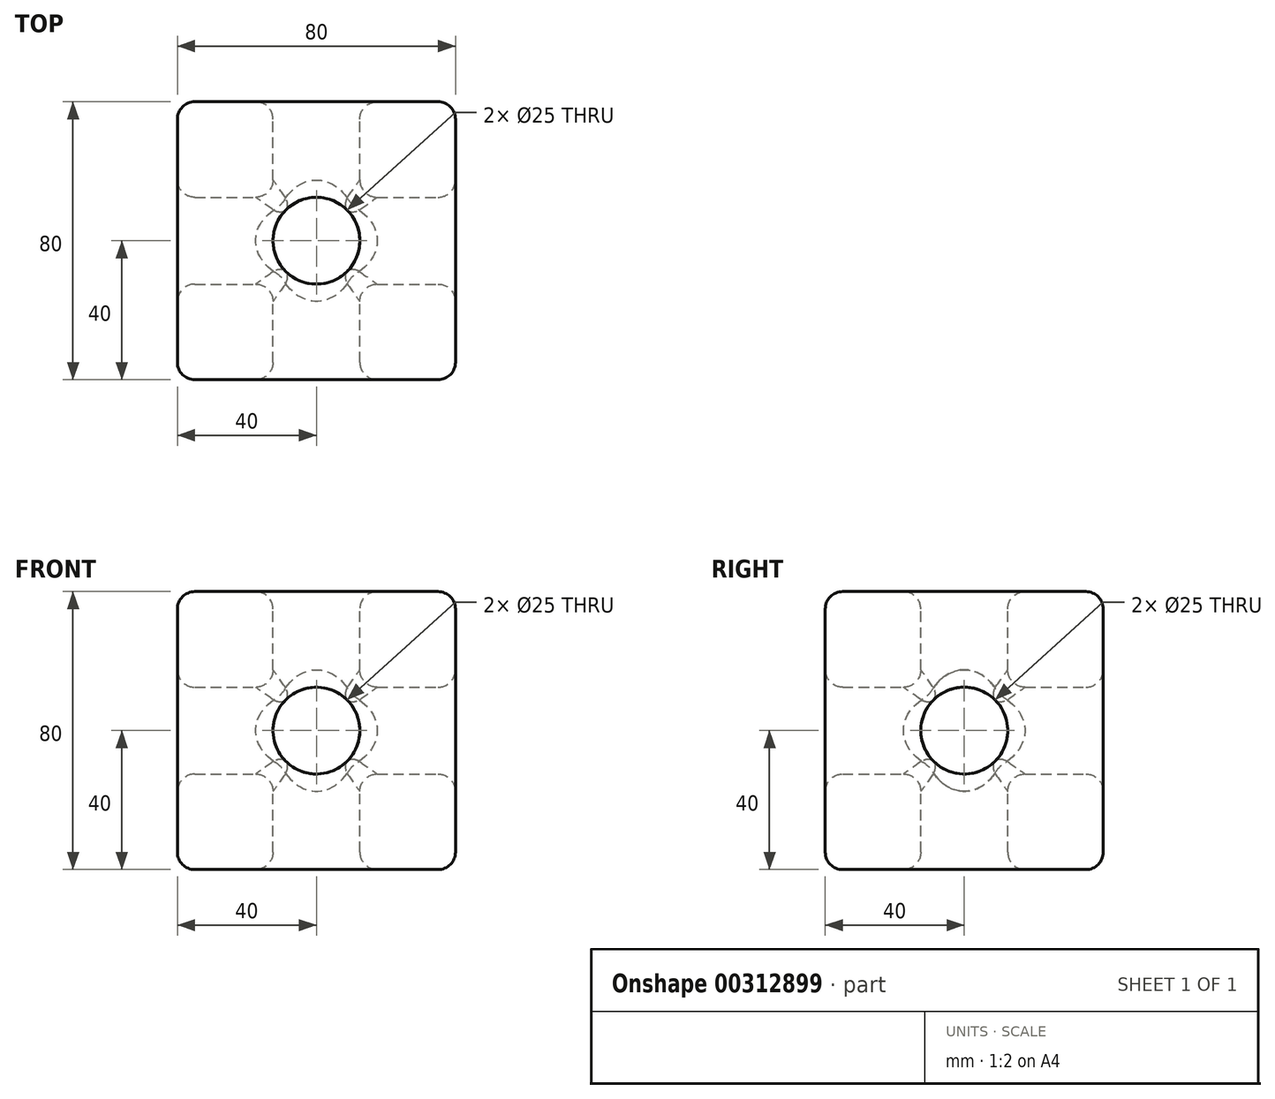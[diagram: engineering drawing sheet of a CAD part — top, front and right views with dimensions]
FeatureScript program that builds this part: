
annotation { "Feature Type Name" : "Feature", "Feature Type Description" : "" }
export const myFeature = defineFeature(function(context is Context, id is Id, definition is map)
    precondition{}
    {
        {
            var Q0;
            Q0=qCreatedBy(makeId("Top.planeOp"),FACE);
            var sketch = newSketch(context, id + "F0", { "sketchPlane" : qUnion([Q0])});
            skLineSegment(sketch, "E0.bottom", {"start": v(40, -40) * mm, "end": v(-40, -40) * mm});
            skLineSegment(sketch, "E0.top", {"start": v(40, 40) * mm, "end": v(-40, 40) * mm});
            skLineSegment(sketch, "E0.left", {"start": v(40, -40) * mm, "end": v(40, 40) * mm});
            skLineSegment(sketch, "E0.right", {"start": v(-40, -40) * mm, "end": v(-40, 40) * mm});
            skPoint(sketch, "E0.middle", {"position": v(0, 0) * mm});
            skSolve(sketch);
        }
        {
            var Q0;
            Q0=makeQuery(id+"F0.imprint","IMPRINT",FACE,{"disambiguationData":[TD([[makeQuery(id+"F0.imprint","IMPRINT",EDGE,{"derivedFrom":sQuery(id+"F0.wireOp",EDGE,"E0.bottom")}),-1.0]])]});
            extrude(context, id + "F1", {"entities" : qUnion([Q0]), "endBound" : BoundingType.SYMMETRIC, "depth" : 80 * mm});
        }
        {
            var Q0;
            Q0=makeQuery(id+"F1.opExtrude","SWEPT_EDGE",EDGE,{"disambiguationData":[OSD([sQuery(id+"F0.wireOp",EDGE,"E0.top"),sQuery(id+"F0.wireOp",EDGE,"E0.left")])]});
            var Q1;
            Q1=makeQuery(id+"F1.opExtrude","CAP_EDGE",EDGE,{"disambiguationData":[OSD([sQuery(id+"F0.wireOp",EDGE,"E0.top")])],"isStart":false});
            var Q2;
            Q2=makeQuery(id+"F1.opExtrude","SWEPT_EDGE",EDGE,{"disambiguationData":[OSD([sQuery(id+"F0.wireOp",EDGE,"E0.top"),sQuery(id+"F0.wireOp",EDGE,"E0.right")])]});
            var Q3;
            Q3=makeQuery(id+"F1.opExtrude","CAP_EDGE",EDGE,{"disambiguationData":[OSD([sQuery(id+"F0.wireOp",EDGE,"E0.top")])],"isStart":true});
            var Q4;
            Q4=makeQuery(id+"F1.opExtrude","SWEPT_EDGE",EDGE,{"disambiguationData":[OSD([sQuery(id+"F0.wireOp",EDGE,"E0.bottom"),sQuery(id+"F0.wireOp",EDGE,"E0.left")])]});
            var Q5;
            Q5=makeQuery(id+"F1.opExtrude","CAP_EDGE",EDGE,{"disambiguationData":[OSD([sQuery(id+"F0.wireOp",EDGE,"E0.left")])],"isStart":true});
            var Q6;
            Q6=makeQuery(id+"F1.opExtrude","CAP_EDGE",EDGE,{"disambiguationData":[OSD([sQuery(id+"F0.wireOp",EDGE,"E0.right")])],"isStart":false});
            var Q7;
            Q7=makeQuery(id+"F1.opExtrude","SWEPT_EDGE",EDGE,{"disambiguationData":[OSD([sQuery(id+"F0.wireOp",EDGE,"E0.bottom"),sQuery(id+"F0.wireOp",EDGE,"E0.right")])]});
            var Q8;
            Q8=makeQuery(id+"F1.opExtrude","CAP_EDGE",EDGE,{"disambiguationData":[OSD([sQuery(id+"F0.wireOp",EDGE,"E0.right")])],"isStart":true});
            var Q9;
            Q9=makeQuery(id+"F1.opExtrude","CAP_EDGE",EDGE,{"disambiguationData":[OSD([sQuery(id+"F0.wireOp",EDGE,"E0.bottom")])],"isStart":false});
            var Q10;
            Q10=makeQuery(id+"F1.opExtrude","CAP_EDGE",EDGE,{"disambiguationData":[OSD([sQuery(id+"F0.wireOp",EDGE,"E0.bottom")])],"isStart":true});
            var Q11;
            Q11=makeQuery(id+"F1.opExtrude","CAP_EDGE",EDGE,{"disambiguationData":[OSD([sQuery(id+"F0.wireOp",EDGE,"E0.left")])],"isStart":false});
            fillet(context, id + "F2", {"entities" : qUnion([Q0, Q1, Q2, Q3, Q4, Q5, Q6, Q7, Q8, Q9, Q10, Q11]), "radius" : 5 * mm, "tangentPropagation" : true, "allowEdgeOverflow" : false});
        }
        {
            var Q0;
            Q0=makeQuery(id+"F1.opExtrude","CAP_FACE",FACE,{"disambiguationData":[OSD([sQuery(id+"F0.wireOp",EDGE,"E0.bottom"),sQuery(id+"F0.wireOp",EDGE,"E0.top"),sQuery(id+"F0.wireOp",EDGE,"E0.left"),sQuery(id+"F0.wireOp",EDGE,"E0.right")])],"isStart":false});
            var sketch = newSketch(context, id + "F3", { "sketchPlane" : qUnion([Q0])});
            skCircle(sketch, "E1", {"center": v(0, 0) * mm, "radius": 12.5 * mm});
            skSolve(sketch);
        }
        {
            var Q0;
            Q0=makeQuery(id+"F3.imprint","IMPRINT",FACE,{"disambiguationData":[TD([[makeQuery(id+"F3.imprint","IMPRINT",EDGE,{"derivedFrom":sQuery(id+"F3.wireOp",EDGE,"E1")}),1.0]])]});
            extrude(context, id + "F4", {"entities" : qUnion([Q0]), "operationType" : NewBodyOperationType.REMOVE, "endBound" : BoundingType.THROUGH_ALL, "oppositeDirection" : true, "depth" : 25 * mm});
        }
        {
            var Q0;
            Q0=makeQuery(id+"F1.opExtrude","SWEPT_FACE",FACE,{"disambiguationData":[OSD([sQuery(id+"F0.wireOp",EDGE,"E0.left")])]});
            var sketch = newSketch(context, id + "F5", { "sketchPlane" : qUnion([Q0])});
            skCircle(sketch, "E2", {"center": v(0, 0) * mm, "radius": 12.5 * mm});
            skSolve(sketch);
        }
        {
            var Q0;
            Q0=makeQuery(id+"F5.imprint","IMPRINT",FACE,{"disambiguationData":[TD([[makeQuery(id+"F5.imprint","IMPRINT",EDGE,{"derivedFrom":sQuery(id+"F5.wireOp",EDGE,"E2")}),1.0]])]});
            extrude(context, id + "F6", {"entities" : qUnion([Q0]), "operationType" : NewBodyOperationType.REMOVE, "endBound" : BoundingType.THROUGH_ALL, "oppositeDirection" : true, "depth" : 25 * mm});
        }
        {
            var Q0;
            Q0=makeQuery(id+"F1.opExtrude","SWEPT_FACE",FACE,{"disambiguationData":[OSD([sQuery(id+"F0.wireOp",EDGE,"E0.top")])]});
            var sketch = newSketch(context, id + "F7", { "sketchPlane" : qUnion([Q0])});
            skCircle(sketch, "E3", {"center": v(0, 0) * mm, "radius": 12.5 * mm});
            skSolve(sketch);
        }
        {
            var Q0;
            Q0=makeQuery(id+"F7.imprint","IMPRINT",FACE,{"disambiguationData":[TD([[makeQuery(id+"F7.imprint","IMPRINT",EDGE,{"derivedFrom":sQuery(id+"F7.wireOp",EDGE,"E3")}),1.0]])]});
            extrude(context, id + "F8", {"entities" : qUnion([Q0]), "operationType" : NewBodyOperationType.REMOVE, "endBound" : BoundingType.THROUGH_ALL, "oppositeDirection" : true, "depth" : 25 * mm});
        }
        {
            var Q0;
            Q0=makeQuery(id+"F8.boolean.opBoolean","INTERSECT",EDGE,{"derivedFrom":[makeQuery(id+"F1.opExtrude","SWEPT_FACE",FACE,{"disambiguationData":[OSD([sQuery(id+"F0.wireOp",EDGE,"E0.bottom")])]}),makeQuery(id+"F8.opExtrude","SWEPT_FACE",FACE,{"disambiguationData":[OSD([sQuery(id+"F7.wireOp",EDGE,"E3")])]})]});
            var Q1;
            Q1=makeQuery(id+"F6.boolean.opBoolean","INTERSECT",EDGE,{"derivedFrom":[makeQuery(id+"F1.opExtrude","SWEPT_FACE",FACE,{"disambiguationData":[OSD([sQuery(id+"F0.wireOp",EDGE,"E0.right")])]}),makeQuery(id+"F6.opExtrude","SWEPT_FACE",FACE,{"disambiguationData":[OSD([sQuery(id+"F5.wireOp",EDGE,"E2")])]})]});
            var Q2;
            Q2=makeQuery(id+"F4.boolean.opBoolean","COPY",EDGE,{"derivedFrom":makeQuery(id+"F4.opExtrude","CAP_EDGE",EDGE,{"disambiguationData":[OSD([sQuery(id+"F3.wireOp",EDGE,"E1")])],"isStart":true})});
            var Q3;
            Q3=makeQuery(id+"F8.boolean.opBoolean","INTERSECT",EDGE,{"disambiguationData":[OD(3.0)],"derivedFrom":[makeQuery(id+"F4.boolean.opBoolean","COPY",FACE,{"derivedFrom":makeQuery(id+"F4.opExtrude","SWEPT_FACE",FACE,{"disambiguationData":[OSD([sQuery(id+"F3.wireOp",EDGE,"E1")])]})}),makeQuery(id+"F8.opExtrude","SWEPT_FACE",FACE,{"disambiguationData":[OSD([sQuery(id+"F7.wireOp",EDGE,"E3")])]})]});
            var Q4;
            Q4=makeQuery(id+"F8.boolean.opBoolean","COPY",EDGE,{"derivedFrom":makeQuery(id+"F8.opExtrude","CAP_EDGE",EDGE,{"disambiguationData":[OSD([sQuery(id+"F7.wireOp",EDGE,"E3")])],"isStart":true})});
            var Q5;
            Q5=makeQuery(id+"F6.boolean.opBoolean","COPY",EDGE,{"derivedFrom":makeQuery(id+"F6.opExtrude","CAP_EDGE",EDGE,{"disambiguationData":[OSD([sQuery(id+"F5.wireOp",EDGE,"E2")])],"isStart":true})});
            var Q6;
            Q6=makeQuery(id+"F4.boolean.opBoolean","INTERSECT",EDGE,{"derivedFrom":[makeQuery(id+"F1.opExtrude","CAP_FACE",FACE,{"disambiguationData":[OSD([sQuery(id+"F0.wireOp",EDGE,"E0.bottom"),sQuery(id+"F0.wireOp",EDGE,"E0.top"),sQuery(id+"F0.wireOp",EDGE,"E0.left"),sQuery(id+"F0.wireOp",EDGE,"E0.right")])],"isStart":true}),makeQuery(id+"F4.opExtrude","SWEPT_FACE",FACE,{"disambiguationData":[OSD([sQuery(id+"F3.wireOp",EDGE,"E1")])]})]});
            var Q7;
            Q7=makeQuery(id+"F8.boolean.opBoolean","INTERSECT",EDGE,{"disambiguationData":[OD(0.0)],"derivedFrom":[makeQuery(id+"F6.boolean.opBoolean","COPY",FACE,{"disambiguationData":[TD([makeQuery(id+"F1.opExtrude","SWEPT_FACE",FACE,{"disambiguationData":[OSD([sQuery(id+"F0.wireOp",EDGE,"E0.right")])]})])],"derivedFrom":makeQuery(id+"F6.opExtrude","SWEPT_FACE",FACE,{"disambiguationData":[OSD([sQuery(id+"F5.wireOp",EDGE,"E2")])]})}),makeQuery(id+"F8.opExtrude","SWEPT_FACE",FACE,{"disambiguationData":[OSD([sQuery(id+"F7.wireOp",EDGE,"E3")])]})]});
            var Q8;
            Q8=makeQuery(id+"F8.boolean.opBoolean","INTERSECT",EDGE,{"disambiguationData":[OD(2.0)],"derivedFrom":[makeQuery(id+"F4.boolean.opBoolean","COPY",FACE,{"derivedFrom":makeQuery(id+"F4.opExtrude","SWEPT_FACE",FACE,{"disambiguationData":[OSD([sQuery(id+"F3.wireOp",EDGE,"E1")])]})}),makeQuery(id+"F8.opExtrude","SWEPT_FACE",FACE,{"disambiguationData":[OSD([sQuery(id+"F7.wireOp",EDGE,"E3")])]})]});
            var Q9;
            Q9=makeQuery(id+"F8.boolean.opBoolean","INTERSECT",EDGE,{"disambiguationData":[OD(1.0)],"derivedFrom":[makeQuery(id+"F6.boolean.opBoolean","COPY",FACE,{"disambiguationData":[TD([makeQuery(id+"F1.opExtrude","SWEPT_FACE",FACE,{"disambiguationData":[OSD([sQuery(id+"F0.wireOp",EDGE,"E0.right")])]})])],"derivedFrom":makeQuery(id+"F6.opExtrude","SWEPT_FACE",FACE,{"disambiguationData":[OSD([sQuery(id+"F5.wireOp",EDGE,"E2")])]})}),makeQuery(id+"F8.opExtrude","SWEPT_FACE",FACE,{"disambiguationData":[OSD([sQuery(id+"F7.wireOp",EDGE,"E3")])]})]});
            var Q10;
            Q10=makeQuery(id+"F8.boolean.opBoolean","COPY",FACE,{"disambiguationData":[TD([makeQuery(id+"F1.opExtrude","SWEPT_FACE",FACE,{"disambiguationData":[OSD([sQuery(id+"F0.wireOp",EDGE,"E0.top")])]})])],"derivedFrom":makeQuery(id+"F8.opExtrude","SWEPT_FACE",FACE,{"disambiguationData":[OSD([sQuery(id+"F7.wireOp",EDGE,"E3")])]})});
            var Q11;
            Q11=makeQuery(id+"F8.boolean.opBoolean","SPLIT",EDGE,{"disambiguationData":[OD(0.0)],"derivedFrom":makeQuery(id+"F6.boolean.opBoolean","INTERSECT",EDGE,{"disambiguationData":[OD(0.0)],"derivedFrom":[makeQuery(id+"F4.boolean.opBoolean","COPY",FACE,{"derivedFrom":makeQuery(id+"F4.opExtrude","SWEPT_FACE",FACE,{"disambiguationData":[OSD([sQuery(id+"F3.wireOp",EDGE,"E1")])]})}),makeQuery(id+"F6.opExtrude","SWEPT_FACE",FACE,{"disambiguationData":[OSD([sQuery(id+"F5.wireOp",EDGE,"E2")])]})]})});
            var Q12;
            {var subQ0=sQuery(id+"F0.wireOp",EDGE,"E0.right");var subQ1=sQuery(id+"F0.wireOp",EDGE,"E0.left");var subQ2=makeQuery(id+"F4.boolean.opBoolean","COPY",FACE,{"derivedFrom":makeQuery(id+"F4.opExtrude","SWEPT_FACE",FACE,{"disambiguationData":[OSD([sQuery(id+"F3.wireOp",EDGE,"E1")])]})});Q12=makeQuery(id+"F8.boolean.opBoolean","SPLIT",FACE,{"disambiguationData":[TD([makeQuery(id+"F1.opExtrude","CAP_FACE",FACE,{"disambiguationData":[OSD([sQuery(id+"F0.wireOp",EDGE,"E0.bottom"),sQuery(id+"F0.wireOp",EDGE,"E0.top"),subQ1,subQ0])],"isStart":true})])],"derivedFrom":subQ2});}
            var Q13;
            Q13=makeQuery(id+"F8.boolean.opBoolean","COPY",FACE,{"disambiguationData":[TD([makeQuery(id+"F1.opExtrude","SWEPT_FACE",FACE,{"disambiguationData":[OSD([sQuery(id+"F0.wireOp",EDGE,"E0.bottom")])]})])],"derivedFrom":makeQuery(id+"F8.opExtrude","SWEPT_FACE",FACE,{"disambiguationData":[OSD([sQuery(id+"F7.wireOp",EDGE,"E3")])]})});
            var Q14;
            {var subQ0=sQuery(id+"F0.wireOp",EDGE,"E0.right");var subQ1=sQuery(id+"F0.wireOp",EDGE,"E0.left");var subQ2=makeQuery(id+"F4.boolean.opBoolean","COPY",FACE,{"derivedFrom":makeQuery(id+"F4.opExtrude","SWEPT_FACE",FACE,{"disambiguationData":[OSD([sQuery(id+"F3.wireOp",EDGE,"E1")])]})});Q14=makeQuery(id+"F8.boolean.opBoolean","SPLIT",FACE,{"disambiguationData":[TD([makeQuery(id+"F1.opExtrude","CAP_FACE",FACE,{"disambiguationData":[OSD([sQuery(id+"F0.wireOp",EDGE,"E0.bottom"),sQuery(id+"F0.wireOp",EDGE,"E0.top"),subQ1,subQ0])],"isStart":false})])],"derivedFrom":subQ2});}
            var Q15;
            Q15=makeQuery(id+"F6.boolean.opBoolean","COPY",FACE,{"disambiguationData":[TD([makeQuery(id+"F1.opExtrude","SWEPT_FACE",FACE,{"disambiguationData":[OSD([sQuery(id+"F0.wireOp",EDGE,"E0.right")])]})])],"derivedFrom":makeQuery(id+"F6.opExtrude","SWEPT_FACE",FACE,{"disambiguationData":[OSD([sQuery(id+"F5.wireOp",EDGE,"E2")])]})});
            var Q16;
            Q16=makeQuery(id+"F6.boolean.opBoolean","COPY",FACE,{"disambiguationData":[TD([makeQuery(id+"F1.opExtrude","SWEPT_FACE",FACE,{"disambiguationData":[OSD([sQuery(id+"F0.wireOp",EDGE,"E0.left")])]})])],"derivedFrom":makeQuery(id+"F6.opExtrude","SWEPT_FACE",FACE,{"disambiguationData":[OSD([sQuery(id+"F5.wireOp",EDGE,"E2")])]})});
            fillet(context, id + "F9", {"entities" : qUnion([Q0, Q1, Q2, Q3, Q4, Q5, Q6, Q7, Q8, Q9, Q10, Q11, Q12, Q13, Q14, Q15, Q16]), "radius" : 5 * mm, "tangentPropagation" : true, "allowEdgeOverflow" : false});
        }
    });
